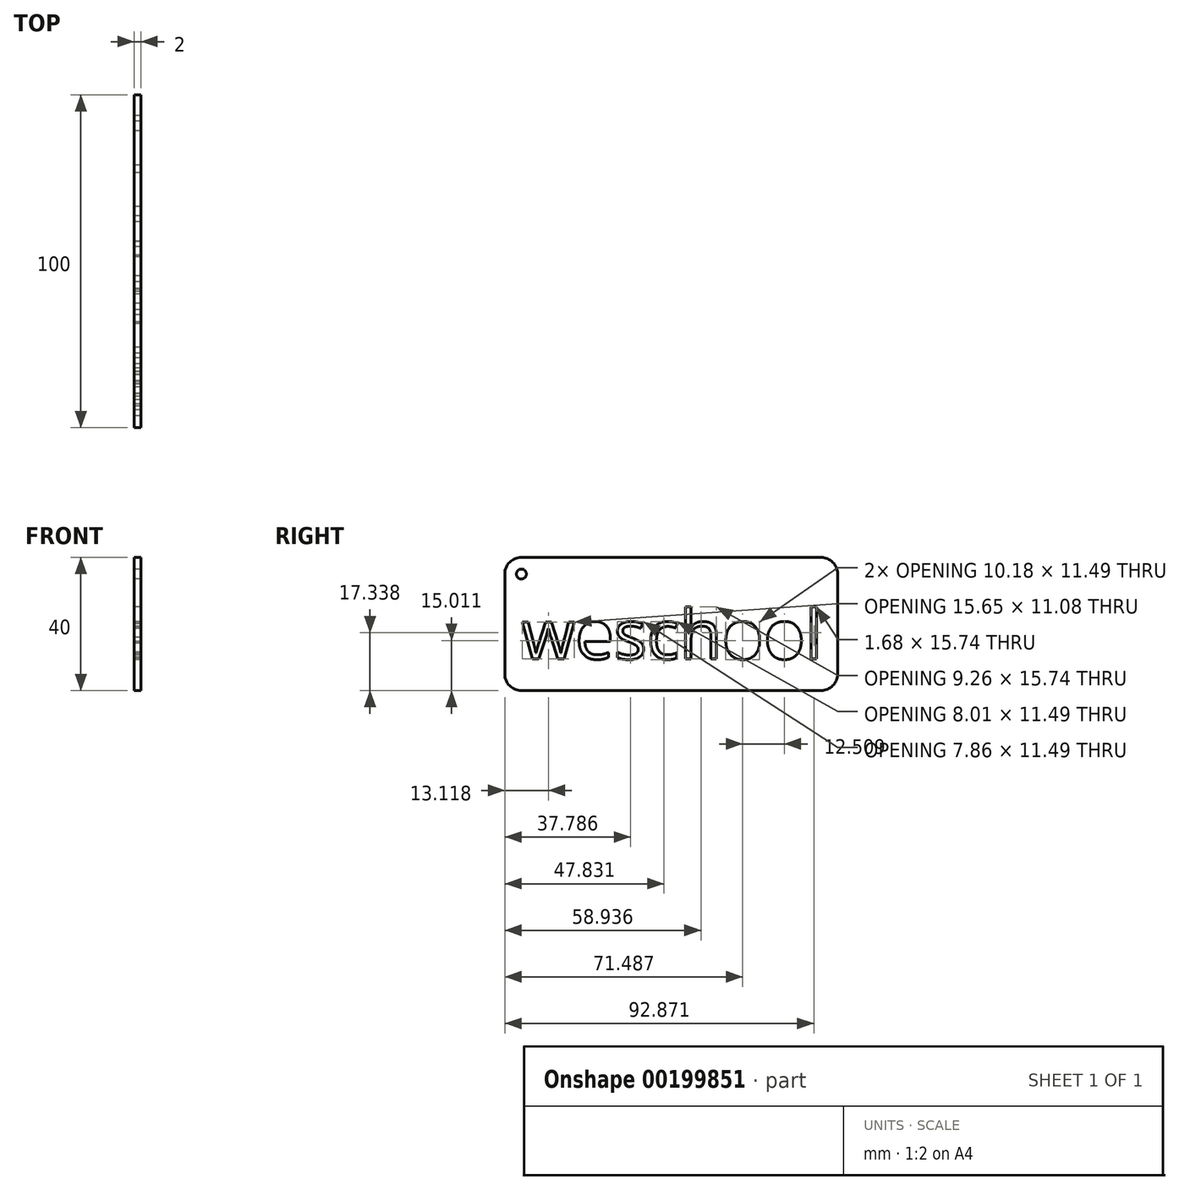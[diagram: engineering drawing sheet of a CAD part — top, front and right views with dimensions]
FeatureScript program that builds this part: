
annotation { "Feature Type Name" : "Feature", "Feature Type Description" : "" }
export const myFeature = defineFeature(function(context is Context, id is Id, definition is map)
    precondition{}
    {
        {
            var Q0;
            Q0=qCreatedBy(makeId("Right.planeOp"),FACE);
            var sketch = newSketch(context, id + "F0", { "sketchPlane" : qUnion([Q0])});
            skLineSegment(sketch, "E0.bottom", {"start": v(5, 0) * mm, "end": v(95, 0) * mm});
            skLineSegment(sketch, "E0.top", {"start": v(5, 40) * mm, "end": v(95, 40) * mm});
            skLineSegment(sketch, "E0.left", {"start": v(0, 5) * mm, "end": v(0, 35) * mm});
            skLineSegment(sketch, "E0.right", {"start": v(100, 5) * mm, "end": v(100, 35) * mm});
            skPoint(sketch, "E1.visualSharp", {"position": v(0, 40) * mm});
            skArc(sketch, "E1.filletArc", {"start": v(5, 40) * mm, "mid": v(1.46, 38.54) * mm, "end": v(0, 35) * mm});
            skPoint(sketch, "E2.visualSharp", {"position": v(0, 0) * mm});
            skArc(sketch, "E2.filletArc", {"start": v(0, 5) * mm, "mid": v(1.46, 1.46) * mm, "end": v(5, 0) * mm});
            skPoint(sketch, "E3.visualSharp", {"position": v(100, 40) * mm});
            skArc(sketch, "E3.filletArc", {"start": v(100, 35) * mm, "mid": v(98.54, 38.54) * mm, "end": v(95, 40) * mm});
            skPoint(sketch, "E4.visualSharp", {"position": v(100, 0) * mm});
            skArc(sketch, "E4.filletArc", {"start": v(95, 0) * mm, "mid": v(98.54, 1.46) * mm, "end": v(100, 5) * mm});
            skText(sketch, "E5", { "text": "weschool\n", "fontName": "OpenSans-Regular.ttf"});
            skCircle(sketch, "E6", {"center": v(5, 35) * mm, "radius": 1.5 * mm});
            const initialGuessF0  = {"E5": [0.00506, 0.00947, 1, 0, 0.01491]};
            skSetInitialGuess(sketch, initialGuessF0);
            skSolve(sketch);
        }
        {
            var Q0;
            Q0 = qSketchRegion(id + "F0", true);
            extrude(context, id + "F1", {"entities" : qUnion([Q0]), "depth" : 2 * mm});
        }
    });
